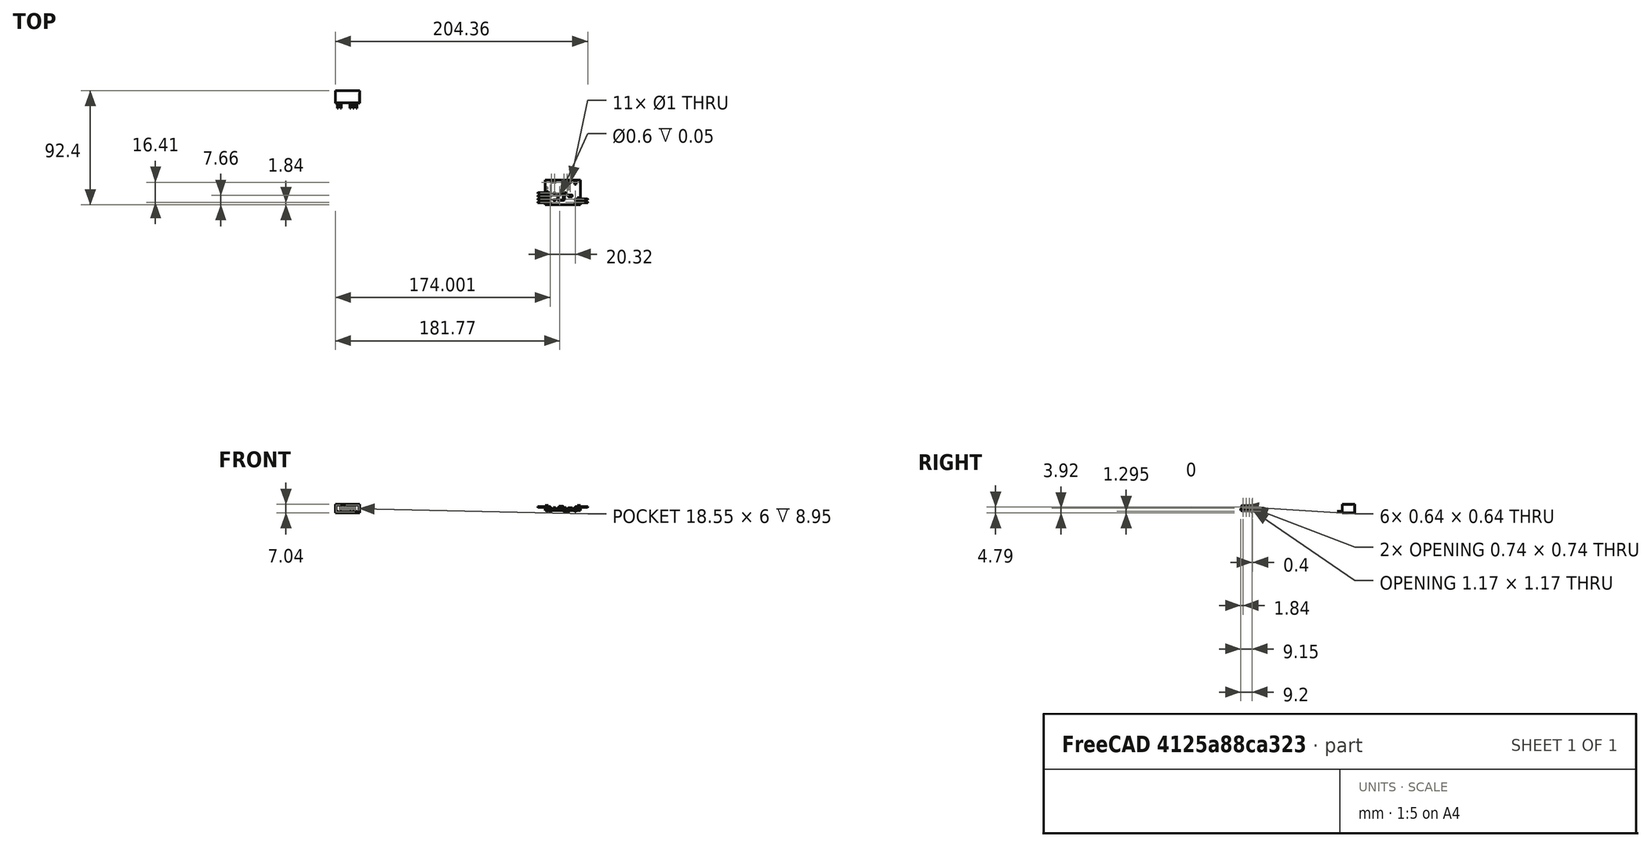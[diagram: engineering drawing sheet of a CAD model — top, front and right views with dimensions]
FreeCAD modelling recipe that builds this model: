
FCSTD DOCUMENT  (FreeCAD 1.0R39285 (Git))
Label: Gate_Driver_Single
License: All rights reserved
LicenseURL: https://en.wikipedia.org/wiki/All_rights_reserved
objects: App::Link×24, Part::Feature×19, App::Part×6, PartDesign::CoordinateSystem×1, Sketcher::SketchObject×1
note: 22 computed .brp shape members not serialized (recipe doc carries the construction recipe); baked Part::Feature solids carry a one-line shape summary decoded from their .brp

FEATURE [PartDesign::CoordinateSystem] Local_CS_6f93
  AttacherType = Attacher::AttachEngine3D
  MapMode = 2
FEATURE [Part::Feature] Pcb_6f93
  shape: bbox 28.5 x 20 x 1.6 mm, 17 faces (baked)
FEATURE [Sketcher::SketchObject] PCB_Sketch_6f93
  ArcFitTolerance = 1e-06
  FullyConstrained = false
  MakeInternals = false
  sketch-geometry (4):
    g0: LineSegment StartX=160.1 StartY=-62.7 StartZ=0 EndX=188.6 EndY=-62.7 EndZ=0
    g1: LineSegment StartX=188.6 StartY=-62.7 StartZ=0 EndX=188.6 EndY=-82.7 EndZ=0
    g2: LineSegment StartX=188.6 StartY=-82.7 StartZ=0 EndX=160.1 EndY=-82.7 EndZ=0
    g3: LineSegment StartX=160.1 StartY=-82.7 StartZ=0 EndX=160.1 EndY=-62.7 EndZ=0
  constraints (4):
    c: Coincident(g2,g3)
    c: Coincident(g0,g3)
    c: Coincident(g1,g2)
    c: Coincident(g0,g1)
FEATURE [App::Part] Board_Geoms_6f93
  Group = -> [Pcb_6f93,PCB_Sketch_6f93]
  Origin = -> Origin
FEATURE [Part::Feature] Shape  label="R2_R_0603_1608Metric_2d54ca4fe2ed"
  Placement = pos=(167.65,-78.85,0) rot=(0,0,1;0rad)
  shape: bbox 1.6 x 0.8 x 0.45 mm, 26 faces (baked)
FEATURE [Part::Feature] Shape001  label="J1_PinHeader_1x04_P254mm_Horizontal_62cb842ff291"
  Placement = pos=(164.171,-80.86,0) rot=(0,0,1;3.14159rad)
  shape: bbox 10.36 x 10.16 x 5.54 mm, 112 faces (baked)
FEATURE [Part::Feature] Shape002  label="R9_R_1206_3216Metric_77f26e49eb4a"
  Placement = pos=(180.25,-75.4,0) rot=(0,0,1;0rad)
  shape: bbox 3.2 x 1.6 x 0.55 mm, 26 faces (baked)
FEATURE [Part::Feature] Part__Feature  label="RKZ-xx2005D_case"
  shape: bbox 19.65 x 10.2 x 7.05 mm, 112 faces (baked)
FEATURE [Part::Feature] Part__Feature001  label="RKZ-xx2005D_pin1(+Vin)"
  shape: bbox 0.5 x 4.6 x 0.25 mm, 6 faces (baked)
FEATURE [Part::Feature] Part__Feature002  label="RKZ-xx2005D_pin7(+Vout)"
  shape: bbox 0.5 x 4.6 x 0.25 mm, 6 faces (baked)
FEATURE [Part::Feature] Part__Feature003  label="RKZ-xx2005D_pin5(-Vout)"
  shape: bbox 0.5 x 4.6 x 0.25 mm, 6 faces (baked)
FEATURE [Part::Feature] Part__Feature004  label="RKZ-xx2005D_pin6(Com)"
  shape: bbox 0.5 x 4.6 x 0.25 mm, 6 faces (baked)
FEATURE [Part::Feature] Part__Feature005  label="RKZ-xx2005D_pin2(-Vin)"
  shape: bbox 0.5 x 4.6 x 0.25 mm, 6 faces (baked)
FEATURE [Part::Feature] Part__Feature006  label="RKZ-xx2005D_potting"
  shape: bbox 18.55 x 8.95 x 6 mm, 6 faces (baked)
FEATURE [App::Part] RKZ_xx2005D  label="U1_RKZ_xx2005D_5871290e3c2f[2]"
  Group = -> [Part__Feature,Part__Feature001,Part__Feature002,Part__Feature003,Part__Feature004,Part__Feature005,Part__Feature006]
  Origin = -> Origin008
  Placement = pos=(173.06,-66.7,0) rot=(1,0,0;1.5708rad)
FEATURE [Part::Feature] Shape003  label="C8_C_0603_1608Metric_c4d86af6c610"
  Placement = pos=(175.95,-73.15,0) rot=(0,0,1;0rad)
  shape: bbox 1.6 x 0.8 x 0.8 mm, 28 faces (baked)
FEATURE [App::Link] R2_R_0603_1608Metric_2d54ca4fe2ed_ln_  label="R1_R_0603_1608Metric_32b94161ff0c"
  LinkPlacement = pos=(167.65,-77.35,0) rot=(0,0,1;0rad)
  LinkedObject = -> Shape
  Placement = pos=(167.65,-77.35,0) rot=(0,0,1;0rad)
FEATURE [App::Link] R9_R_1206_3216Metric_77f26e49eb4a_ln_  label="R8_R_1206_3216Metric_2ab3c3f53bdb"
  LinkPlacement = pos=(180.25,-80,0) rot=(0,0,1;0rad)
  LinkedObject = -> Shape002
  Placement = pos=(180.25,-80,0) rot=(0,0,1;0rad)
FEATURE [Part::Feature] Shape004  label="L1_L_0603_1608Metric_df87eb78f64c"
  Placement = pos=(167.6,-73.55,0) rot=(0,0,1;0rad)
  shape: bbox 1.6 x 0.8 x 0.8 mm, 28 faces (baked)
FEATURE [App::Link] C8_C_0603_1608Metric_c4d86af6c610_ln_  label="C7_C_0603_1608Metric_7951df6ea563"
  LinkPlacement = pos=(176.05,-80.1,0) rot=(0,0,1;0rad)
  LinkedObject = -> Shape003
  Placement = pos=(176.05,-80.1,0) rot=(0,0,1;0rad)
FEATURE [App::Link] C8_C_0603_1608Metric_c4d86af6c610_ln_001  label="C6_C_0603_1608Metric_30922a0b8c5d"
  LinkPlacement = pos=(169.162,-72.05,0) rot=(0,0,1;3.14159rad)
  LinkedObject = -> Shape003
  Placement = pos=(169.162,-72.05,0) rot=(0,0,1;3.14159rad)
FEATURE [Part::Feature] Shape005  label="R3_R_0805_2012Metric_3cebb0b8ae29"
  Placement = pos=(184.5,-65.05,0) rot=(0,0,1;1.5708rad)
  shape: bbox 1.2 x 2 x 0.45 mm, 26 faces (baked)
FEATURE [App::Link] C8_C_0603_1608Metric_c4d86af6c610_ln_002  label="C3_C_0603_1608Metric_57c32b27324a"
  LinkPlacement = pos=(167.65,-80.35,0) rot=(0,0,1;3.14159rad)
  LinkedObject = -> Shape003
  Placement = pos=(167.65,-80.35,0) rot=(0,0,1;3.14159rad)
FEATURE [App::Link] R9_R_1206_3216Metric_77f26e49eb4a_ln_001  label="R7_R_1206_3216Metric_a32205590e4e"
  LinkPlacement = pos=(180.25,-77.7,0) rot=(0,0,1;0rad)
  LinkedObject = -> Shape002
  Placement = pos=(180.25,-77.7,0) rot=(0,0,1;0rad)
FEATURE [App::Link] R9_R_1206_3216Metric_77f26e49eb4a_ln_002  label="R10_R_1206_3216Metric_528fcbde50e6"
  LinkPlacement = pos=(180.25,-73.1,0) rot=(0,0,1;0rad)
  LinkedObject = -> Shape002
  Placement = pos=(180.25,-73.1,0) rot=(0,0,1;0rad)
FEATURE [App::Link] C8_C_0603_1608Metric_c4d86af6c610_ln_003  label="C2_C_0603_1608Metric_14af21b942a6"
  LinkPlacement = pos=(167.65,-75.85,0) rot=(0,0,1;3.14159rad)
  LinkedObject = -> Shape003
  Placement = pos=(167.65,-75.85,0) rot=(0,0,1;3.14159rad)
FEATURE [Part::Feature] Shape006  label="U2_SOIC_8_39x49mm_P127mm_12a9d7132351"
  Placement = pos=(173.05,-76.65,0) rot=(0,0,1;0rad)
  shape: bbox 6 x 4.9 x 1.75 mm, 156 faces (baked)
FEATURE [Part::Feature] Shape007  label="J2_PinHeader_1x02_P254mm_Horizontal_2606b46b36f0"
  Placement = pos=(184.491,-78.32,0) rot=(0,0,1;0rad)
  shape: bbox 10.36 x 5.08 x 5.54 mm, 58 faces (baked)
FEATURE [App::Part] Top_6f93
  Group = -> [Shape,Shape001,Shape002,RKZ_xx2005D,Shape003,R2_R_0603_1608Metric_2d54ca4fe2ed_ln_,R9_R_1206_3216Metric_77f26e49eb4a_ln_,Shape004,C8_C_0603_1608Metric_c4d86af6c610_ln_,C8_C_0603_1608Metric_c4d86af6c610_ln_001,Shape005,C8_C_0603_1608Metric_c4d86af6c610_ln_002,R9_R_1206_3216Metric_77f26e49eb4a_ln_001,R9_R_1206_3216Metric_77f26e49eb4a_ln_002,C8_C_0603_1608Metric_c4d86af6c610_ln_003,Shape006,Shape007]
  Origin = -> Origin003
FEATURE [App::Link] R2_R_0603_1608Metric_2d54ca4fe2ed_ln_001  label="R11_R_0603_1608Metric_4e979ecce863"
  LinkPlacement = pos=(161.75,-65.8375,-1.6) rot=(0.707107,0.707107,0;3.14159rad)
  LinkedObject = -> Shape
  Placement = pos=(161.75,-65.8375,-1.6) rot=(0.707107,0.707107,0;3.14159rad)
FEATURE [Part::Feature] Shape008  label="C12_C_0805_2012Metric_f5f1997052fd"
  Placement = pos=(176.4,-73.5,-1.6) rot=(1,0,0;3.14159rad)
  shape: bbox 2 x 1.25 x 1.25 mm, 28 faces (baked)
FEATURE [App::Link] C8_C_0603_1608Metric_c4d86af6c610_ln_004  label="C13_C_0603_1608Metric_a92657ceca87"
  LinkPlacement = pos=(175.95,-70.4375,-1.6) rot=(0,1,0;3.14159rad)
  LinkedObject = -> Shape003
  Placement = pos=(175.95,-70.4375,-1.6) rot=(0,1,0;3.14159rad)
FEATURE [App::Link] C12_C_0805_2012Metric_f5f1997052fd_ln_  label="C16_C_0805_2012Metric_42320fc42582"
  LinkPlacement = pos=(176.4,-77.5,-1.6) rot=(1,0,0;3.14159rad)
  LinkedObject = -> Shape008
  Placement = pos=(176.4,-77.5,-1.6) rot=(1,0,0;3.14159rad)
FEATURE [App::Link] C12_C_0805_2012Metric_f5f1997052fd_ln_001  label="C10_C_0805_2012Metric_3e539c29efa7"
  LinkPlacement = pos=(176.15,-66.0375,-1.6) rot=(0,1,0;3.14159rad)
  LinkedObject = -> Shape008
  Placement = pos=(176.15,-66.0375,-1.6) rot=(0,1,0;3.14159rad)
FEATURE [App::Link] C12_C_0805_2012Metric_f5f1997052fd_ln_002  label="C11_C_0805_2012Metric_0803004ee581"
  LinkPlacement = pos=(176.4,-79.5,-1.6) rot=(1,0,0;3.14159rad)
  LinkedObject = -> Shape008
  Placement = pos=(176.4,-79.5,-1.6) rot=(1,0,0;3.14159rad)
FEATURE [App::Link] C8_C_0603_1608Metric_c4d86af6c610_ln_005  label="C14_C_0603_1608Metric_6dff1493bc70"
  LinkPlacement = pos=(186.6,-79.6,-1.6) rot=(0.707107,0.707107,0;3.14159rad)
  LinkedObject = -> Shape003
  Placement = pos=(186.6,-79.6,-1.6) rot=(0.707107,0.707107,0;3.14159rad)
FEATURE [App::Link] R2_R_0603_1608Metric_2d54ca4fe2ed_ln_002  label="R6_R_0603_1608Metric_18c2b8362bf6"
  LinkPlacement = pos=(175.95,-67.7875,-1.6) rot=(1,0,0;3.14159rad)
  LinkedObject = -> Shape
  Placement = pos=(175.95,-67.7875,-1.6) rot=(1,0,0;3.14159rad)
FEATURE [App::Link] C8_C_0603_1608Metric_c4d86af6c610_ln_006  label="C15_C_0603_1608Metric_f8f0652e5bc0"
  LinkPlacement = pos=(166.55,-66.1,-1.6) rot=(1,0,0;3.14159rad)
  LinkedObject = -> Shape003
  Placement = pos=(166.55,-66.1,-1.6) rot=(1,0,0;3.14159rad)
FEATURE [App::Link] R2_R_0603_1608Metric_2d54ca4fe2ed_ln_003  label="R5_R_0603_1608Metric_41ea8f9ed5fc"
  LinkPlacement = pos=(181.2,-68.7875,-1.6) rot=(0.707107,-0.707107,0;3.14159rad)
  LinkedObject = -> Shape
  Placement = pos=(181.2,-68.7875,-1.6) rot=(0.707107,-0.707107,0;3.14159rad)
FEATURE [App::Link] C12_C_0805_2012Metric_f5f1997052fd_ln_003  label="C9_C_0805_2012Metric_9de5ad782305"
  LinkPlacement = pos=(179.95,-66.0375,-1.6) rot=(0,1,0;3.14159rad)
  LinkedObject = -> Shape008
  Placement = pos=(179.95,-66.0375,-1.6) rot=(0,1,0;3.14159rad)
FEATURE [Part::Feature] Shape009  label="D1_LED_0603_1608Metric_c1b8b79c1f83"
  Placement = pos=(161.7,-69.15,-1.6) rot=(0.707107,-0.707107,0;3.14159rad)
  shape: bbox 0.8 x 1.6 x 1.1 mm, 50 faces (baked)
FEATURE [App::Link] C12_C_0805_2012Metric_f5f1997052fd_ln_004  label="C1_C_0805_2012Metric_8f30ed5e9449"
  LinkPlacement = pos=(166.75,-67.85,-1.6) rot=(1,0,0;3.14159rad)
  LinkedObject = -> Shape008
  Placement = pos=(166.75,-67.85,-1.6) rot=(1,0,0;3.14159rad)
FEATURE [App::Link] L1_L_0603_1608Metric_df87eb78f64c_ln_  label="L2_L_0603_1608Metric_09f8cb0d91ba"
  LinkPlacement = pos=(164.1,-67.15,-1.6) rot=(0.707107,0.707107,0;3.14159rad)
  LinkedObject = -> Shape004
  Placement = pos=(164.1,-67.15,-1.6) rot=(0.707107,0.707107,0;3.14159rad)
FEATURE [App::Link] R2_R_0603_1608Metric_2d54ca4fe2ed_ln_004  label="R4_R_0603_1608Metric_c49fec0b3b66"
  LinkPlacement = pos=(182.7,-68.7875,-1.6) rot=(0.707107,0.707107,0;3.14159rad)
  LinkedObject = -> Shape
  Placement = pos=(182.7,-68.7875,-1.6) rot=(0.707107,0.707107,0;3.14159rad)
FEATURE [App::Link] C12_C_0805_2012Metric_f5f1997052fd_ln_005  label="C5_C_0805_2012Metric_f0284871c668"
  LinkPlacement = pos=(161.9,-74.5,-1.6) rot=(0.707107,-0.707107,0;3.14159rad)
  LinkedObject = -> Shape008
  Placement = pos=(161.9,-74.5,-1.6) rot=(0.707107,-0.707107,0;3.14159rad)
FEATURE [App::Link] C12_C_0805_2012Metric_f5f1997052fd_ln_006  label="C17_C_0805_2012Metric_56391f6a3c2a"
  LinkPlacement = pos=(176.4,-75.5,-1.6) rot=(1,0,0;3.14159rad)
  LinkedObject = -> Shape008
  Placement = pos=(176.4,-75.5,-1.6) rot=(1,0,0;3.14159rad)
FEATURE [Part::Feature] Shape010  label="U3_SOT_23_1686a0ddb1d1"
  Placement = pos=(178.512,-69.0875,-1.6) rot=(0,1,0;3.14159rad)
  shape: bbox 2.5 x 3 x 1.2 mm, 76 faces (baked)
FEATURE [App::Link] C12_C_0805_2012Metric_f5f1997052fd_ln_007  label="C4_C_0805_2012Metric_d4de7a310149"
  LinkPlacement = pos=(169.162,-72.05,-1.6) rot=(0,1,0;3.14159rad)
  LinkedObject = -> Shape008
  Placement = pos=(169.162,-72.05,-1.6) rot=(0,1,0;3.14159rad)
FEATURE [App::Part] Bot_6f93
  Group = -> [R2_R_0603_1608Metric_2d54ca4fe2ed_ln_001,Shape008,C8_C_0603_1608Metric_c4d86af6c610_ln_004,C12_C_0805_2012Metric_f5f1997052fd_ln_,C12_C_0805_2012Metric_f5f1997052fd_ln_001,C12_C_0805_2012Metric_f5f1997052fd_ln_002,C8_C_0603_1608Metric_c4d86af6c610_ln_005,R2_R_0603_1608Metric_2d54ca4fe2ed_ln_002,C8_C_0603_1608Metric_c4d86af6c610_ln_006,R2_R_0603_1608Metric_2d54ca4fe2ed_ln_003,+9 more]
  Origin = -> Origin004
FEATURE [App::Part] Step_Models_6f93
  Group = -> [Top_6f93,Bot_6f93]
  Origin = -> Origin002
FEATURE [App::Part] Board_6f93  label="Gate_Driver_Single"
  Group = -> [Local_CS_6f93,Board_Geoms_6f93,Step_Models_6f93]
  Origin = -> Origin001
